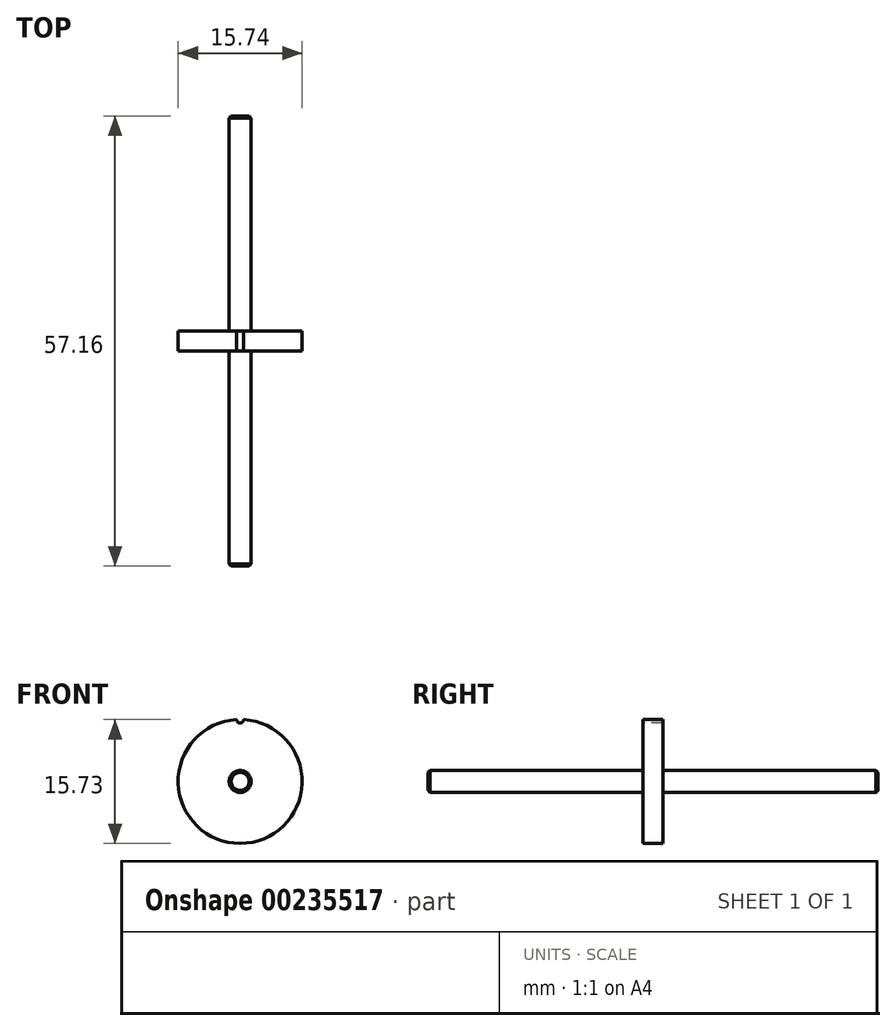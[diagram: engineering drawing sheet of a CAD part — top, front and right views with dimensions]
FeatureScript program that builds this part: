
annotation { "Feature Type Name" : "Feature", "Feature Type Description" : "" }
export const myFeature = defineFeature(function(context is Context, id is Id, definition is map)
    precondition{}
    {
        {
            var Q0;
            Q0=qCreatedBy(makeId("Front.planeOp"),FACE);
            var sketch = newSketch(context, id + "F0", { "sketchPlane" : qUnion([Q0])});
            skCircle(sketch, "E0", {"center": v(0, 0) * mm, "radius": 7.87 * mm});
            skCircle(sketch, "E1", {"center": v(0, 0) * mm, "radius": 6.99 * mm});
            skCircle(sketch, "E2", {"center": v(0, 0) * mm, "radius": 1.4 * mm});
            skSolve(sketch);
        }
        {
            var Q0;
            Q0=makeQuery(id+"F0.imprint","IMPRINT",FACE,{"disambiguationData":[TD([[makeQuery(id+"F0.imprint","IMPRINT",EDGE,{"derivedFrom":sQuery(id+"F0.wireOp",EDGE,"E1")}),1.0]])]});
            var Q1;
            Q1=makeQuery(id+"F0.imprint","IMPRINT",FACE,{"disambiguationData":[TD([[makeQuery(id+"F0.imprint","IMPRINT",EDGE,{"derivedFrom":sQuery(id+"F0.wireOp",EDGE,"E0")}),1.0]])]});
            extrude(context, id + "F1", {"entities" : qUnion([Q0, Q1]), "endBound" : BoundingType.SYMMETRIC, "depth" : 2.54 * mm});
        }
        {
            var Q0;
            Q0=makeQuery(id+"F0.imprint","IMPRINT",FACE,{"disambiguationData":[TD([[makeQuery(id+"F0.imprint","IMPRINT",EDGE,{"derivedFrom":sQuery(id+"F0.wireOp",EDGE,"E2")}),1.0]])]});
            extrude(context, id + "F2", {"entities" : qUnion([Q0]), "operationType" : NewBodyOperationType.ADD, "endBound" : BoundingType.SYMMETRIC, "depth" : 57.15 * mm});
        }
        {
            var Q0;
            Q0=makeQuery(id+"F1.opExtrude","CAP_FACE",FACE,{"disambiguationData":[OSD([sQuery(id+"F0.wireOp",EDGE,"E0"),sQuery(id+"F0.wireOp",EDGE,"E2")])],"isStart":false});
            var sketch = newSketch(context, id + "F3", { "sketchPlane" : qUnion([Q0])});
            skCircle(sketch, "E3", {"center": v(0, 0) * mm, "radius": 7.43 * mm, "construction": true});
            skArc(sketch, "E4", {"start": v(-0.44, 7.86) * mm, "mid": v(0, 7.43) * mm, "end": v(0.44, 7.86) * mm});
            skArc(sketch, "E5.0", {"start": v(0.44, 7.86) * mm, "mid": v(0, 7.87) * mm, "end": v(-0.44, 7.86) * mm});
            skSolve(sketch);
        }
        {
            var Q0;
            Q0 = qSketchRegion(id + "F3", true);
            extrude(context, id + "F4", {"entities" : qUnion([Q0]), "operationType" : NewBodyOperationType.REMOVE, "oppositeDirection" : true, "depth" : 25.4 * mm});
        }
        {
            var Q0;
            Q0=makeQuery(id+"F2.opExtrude","CAP_EDGE",EDGE,{"disambiguationData":[OSD([sQuery(id+"F0.wireOp",EDGE,"E2")])],"isStart":false});
            var Q1;
            Q1=makeQuery(id+"F2.opExtrude","CAP_EDGE",EDGE,{"disambiguationData":[OSD([sQuery(id+"F0.wireOp",EDGE,"E2")])],"isStart":true});
            chamfer(context, id + "F5", {"entities" : qUnion([Q0, Q1]), "width" : 0.25 * mm, "tangentPropagation" : true});
        }
    });
